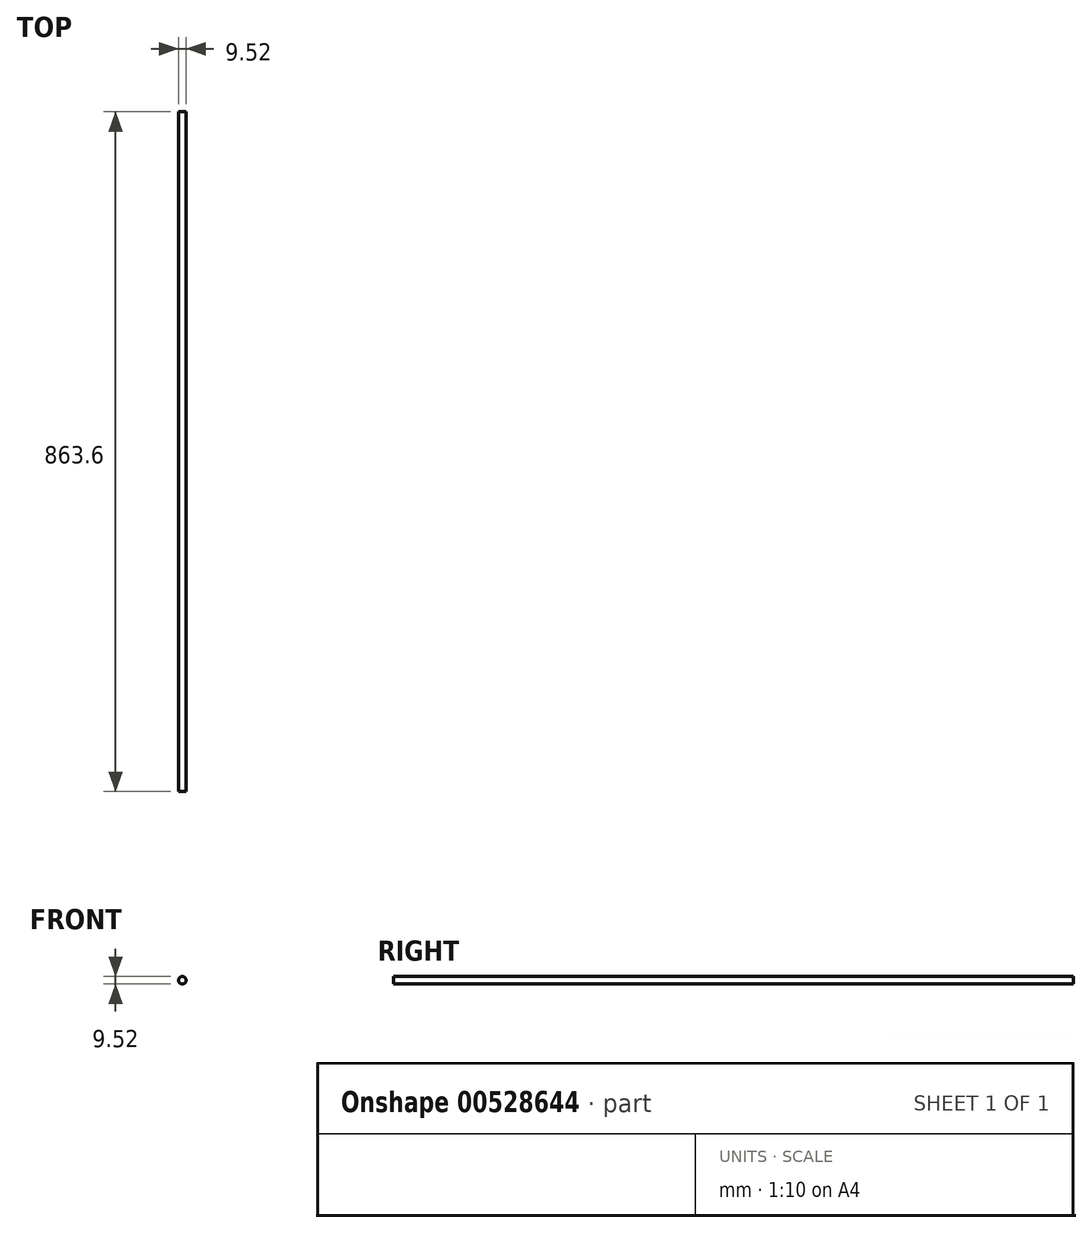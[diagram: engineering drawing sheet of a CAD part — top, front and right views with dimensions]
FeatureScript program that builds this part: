
annotation { "Feature Type Name" : "Feature", "Feature Type Description" : "" }
export const myFeature = defineFeature(function(context is Context, id is Id, definition is map)
    precondition{}
    {
        {
            var Q0;
            Q0=qCreatedBy(makeId("Front.planeOp"),FACE);
            var sketch = newSketch(context, id + "F0", { "sketchPlane" : qUnion([Q0])});
            skCircle(sketch, "E0", {"center": v(0, 0) * mm, "radius": 4.76 * mm});
            skSolve(sketch);
        }
        {
            var Q0;
            Q0=makeQuery(id+"F0.imprint","IMPRINT",FACE,{"disambiguationData":[TD([[makeQuery(id+"F0.imprint","IMPRINT",EDGE,{"derivedFrom":sQuery(id+"F0.wireOp",EDGE,"E0")}),1.0]])]});
            extrude(context, id + "F1", {"entities" : qUnion([Q0]), "depth" : 863.6 * mm, "offsetDistance" : 25.4 * mm});
        }
    });
